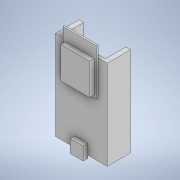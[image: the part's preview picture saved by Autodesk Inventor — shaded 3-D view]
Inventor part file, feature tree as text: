
AUTODESK INVENTOR PART (.ipt)
format: ipt  version: 2022 (Build 260153000, 153)  size: 147,968 bytes
history: native  units: mm
features: extrude x5, sketch x5, other x1
ambient origin geometry x8: Origin, YZ Plane, XZ Plane, XY Plane, X Axis, Y Axis, Z Axis, Center Point
bodies: Body1 (feature_tree)
feature tree (11):
  other  "ソリッド1"
  extrude  "押し出し1"  Depth=27.94mm
  extrude  "押し出し2"  Depth=48.26mm
  extrude  "押し出し3"  Depth=1.6mm TaperAngle=0.0deg
  extrude  "押し出し4"  Depth=25.4mm
  extrude  "押し出し5"  Depth=2.54mm
  sketch  "スケッチ1"
  sketch  "スケッチ2"
  sketch  "スケッチ3"
  sketch  "スケッチ4"
  sketch  "スケッチ5"
